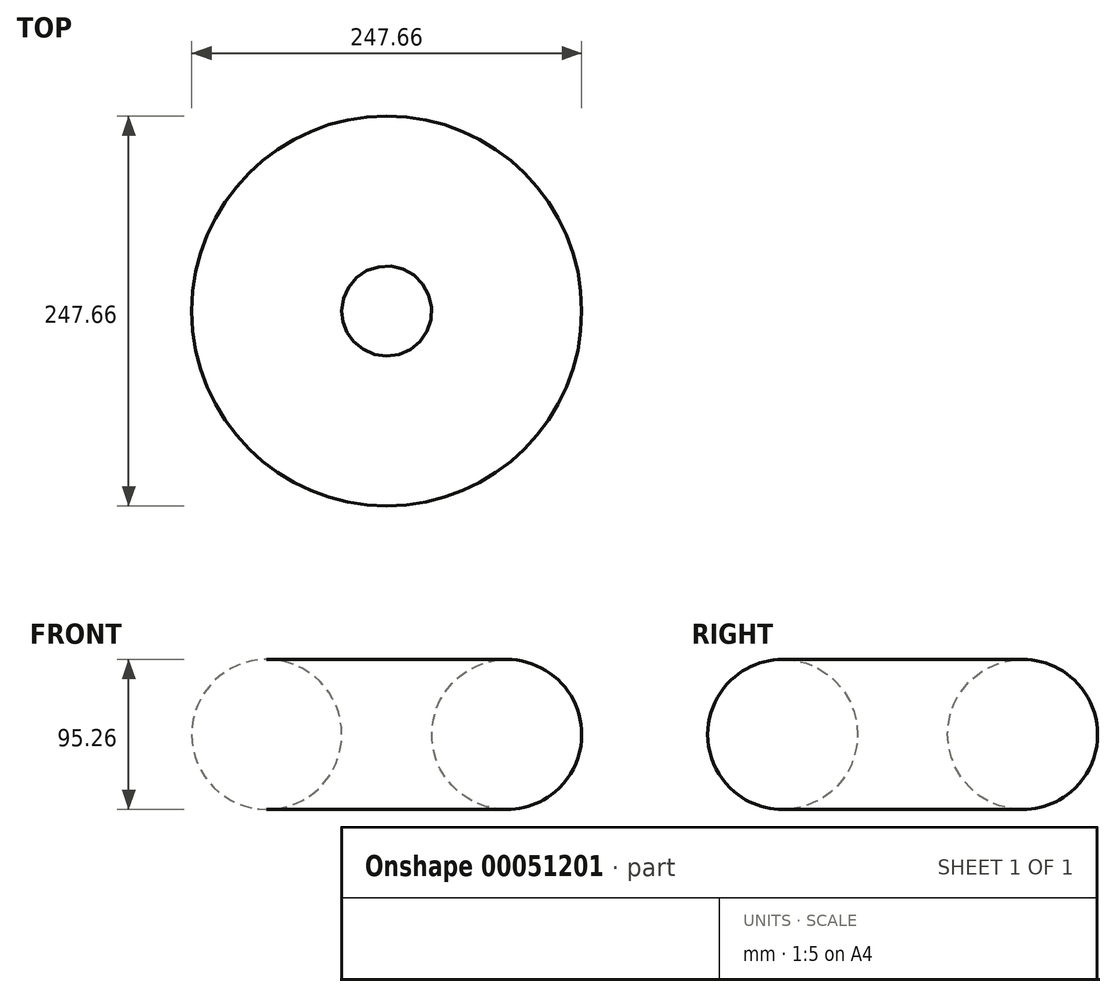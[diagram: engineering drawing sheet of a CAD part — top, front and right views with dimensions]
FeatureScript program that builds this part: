
annotation { "Feature Type Name" : "Feature", "Feature Type Description" : "" }
export const myFeature = defineFeature(function(context is Context, id is Id, definition is map)
    precondition{}
    {
        {
            var Q0;
            Q0=qCreatedBy(makeId("Front.planeOp"),FACE);
            var sketch = newSketch(context, id + "F0", { "sketchPlane" : qUnion([Q0])});
            skLineSegment(sketch, "E0", {"start": v(0, 0) * mm, "end": v(0, 315.1) * mm});
            skCircle(sketch, "E1", {"center": v(76.2, 0) * mm, "radius": 47.63 * mm});
            skSolve(sketch);
        }
        {
            var Q0;
            Q0 = qSketchRegion(id + "F0", true);
            var Q1;
            Q1=sQuery(id+"F0.wireOp",EDGE,"E0");
            revolve(context, id + "F1", {"entities" : qUnion([Q0]), "axis" : qUnion([Q1]), "revolveType" : RevolveType.FULL});
        }
        {
            var Q0;
            Q0=qCreatedBy(makeId("Top.planeOp"),FACE);
            cPlane(context, id + "F2", {"entities" : qUnion([Q0]), "cplaneType" : CPlaneType.OFFSET, "offset" : 152.4 * mm, "width" : 152.4 * mm, "height" : 152.4 * mm});
        }
    });
